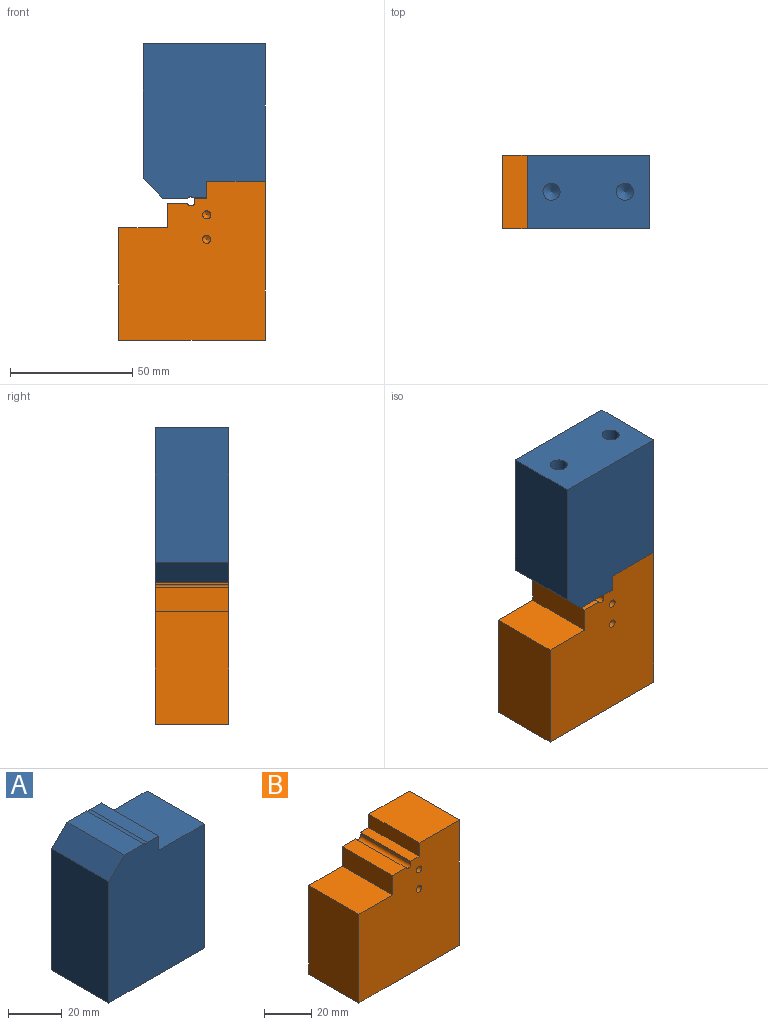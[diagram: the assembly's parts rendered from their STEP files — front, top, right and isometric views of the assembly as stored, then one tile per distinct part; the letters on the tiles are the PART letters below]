
ASSEMBLY  parts=2 mates=1
PART A: 15 faces, bbox 50x30x63.2 mm
  f0: cylinder r=1.5mm len=30mm, axis (0,-1,0), area 61.4mm2, adj f1,f2,f5,f10
  f1: plane 63.15x50mm, normal (0,-1,0), area 2958.6mm2, adj f0,f3,f4,f5,f6,f7,f8,f9
  f2: plane 63.15x50mm, normal (0,1,0), area 2958.6mm2, adj f0,f3,f4,f5,f6,f7,f8,f9
  f3: plane 56.3x30mm, normal (1,0,0), area 1689mm2, adj f1,f2,f4,f8
  f4: plane 50x30mm, normal (0,0,-1), area 1423mm2, adj f1,f2,f3,f6,f12,f14
  f5: plane 30x10.28mm, normal (0,0,1), area 308.5mm2, adj f0,f1,f2,f9
  f6: plane 55.15x30mm, normal (-1,0,0), area 1654.5mm2, adj f1,f2,f4,f9
  f7: plane 30x6.55mm, normal (1,0,0), area 196.5mm2, adj f1,f2,f8,f10
  f8: plane 30x24mm, normal (0,0,1), area 720mm2, adj f1,f2,f3,f7
  f9: plane 30x8mm, normal (-0.71,0,0.71), area 339.4mm2, adj f1,f2,f5,f6
  f10: plane 30x5.85mm, normal (0,0,1), area 175.6mm2, adj f0,f1,f2,f7
  f11: cone r=0mm half-angle=59deg, axis (0,0,-1), area 44.9mm2, adj f12
  f12: cylinder r=3.5mm len=15mm, axis (0,0,-1), area 329.9mm2, adj f4,f11
  f13: cone r=0mm half-angle=59deg, axis (0,0,-1), area 44.9mm2, adj f14
  f14: cylinder r=3.5mm len=15mm, axis (0,0,-1), area 329.9mm2, adj f4,f13
PART B: 25 faces, bbox 60x30x65 mm
  f0: plane 30x8.19mm, normal (0,0,1), area 245.6mm2, adj f6,f7,f9,f12
  f1: plane 30x24mm, normal (0,0,1), area 720mm2, adj f4,f6,f7,f11
  f2: plane 30x0.96mm, normal (-1,0,0), area 28.8mm2, adj f6,f7,f10,f12
  f3: plane 60x30mm, normal (0,0,-1), area 1727.4mm2, adj f4,f5,f6,f7,f22,f24
  f4: plane 65x30mm, normal (1,0,0), area 1950mm2, adj f1,f3,f6,f7
  f5: plane 46.05x30mm, normal (-1,0,0), area 1381.5mm2, adj f3,f6,f7,f8
  f6: plane 65x60mm, normal (0,-1,0), area 3368.6mm2, adj f0,f1,f2,f3,f4,f5,f8,f9
  f7: plane 65x60mm, normal (0,1,0), area 3368.6mm2, adj f0,f1,f2,f3,f4,f5,f8,f9
  f8: plane 30x20mm, normal (0,0,1), area 600mm2, adj f5,f6,f7,f9
  f9: plane 30x10mm, normal (-1,0,0), area 300mm2, adj f0,f6,f7,f8
  f10: plane 30x5mm, normal (0,0,1), area 150mm2, adj f2,f6,f7,f11
  f11: plane 30x6.95mm, normal (-1,0,0), area 208.5mm2, adj f1,f6,f7,f10
  f12: cylinder r=1.5mm len=30mm, axis (0,-1,0), area 142.6mm2, adj f0,f2,f6,f7
  f13: cone r=0mm half-angle=59deg, axis (0,-1,0), area 10mm2, adj f14
  f14: cylinder r=1.65mm len=12mm, axis (0,-1,0), area 124.4mm2, adj f6,f13
  f15: cone r=0mm half-angle=59deg, axis (0,-1,0), area 10mm2, adj f16
  f16: cylinder r=1.65mm len=12mm, axis (0,-1,0), area 124.4mm2, adj f6,f15
  f17: cone r=0mm half-angle=59deg, axis (0,1,0), area 10mm2, adj f18
  f18: cylinder r=1.65mm len=12mm, axis (0,1,0), area 124.4mm2, adj f7,f17
  f19: cone r=0mm half-angle=59deg, axis (0,1,0), area 10mm2, adj f20
  f20: cylinder r=1.65mm len=12mm, axis (0,1,0), area 124.4mm2, adj f7,f19
  f21: cone r=0mm half-angle=59deg, axis (0,0,-1), area 42.4mm2, adj f22
  f22: cylinder r=3.4mm len=20mm, axis (0,0,-1), area 427.3mm2, adj f3,f21
  f23: cone r=0mm half-angle=59deg, axis (0,0,-1), area 42.4mm2, adj f24
  f24: cylinder r=3.4mm len=20mm, axis (0,0,-1), area 427.3mm2, adj f3,f23
PLACE A rot(axis=(1,0,0),180deg) t=(2.36,-14.98,67.67)mm
PLACE B t=(-7.64,15.02,-10.53)mm
MATE fastened A.f8 <-> B.f1  axis (0,0,-1) through (17.55,0.02,32.92)mm
